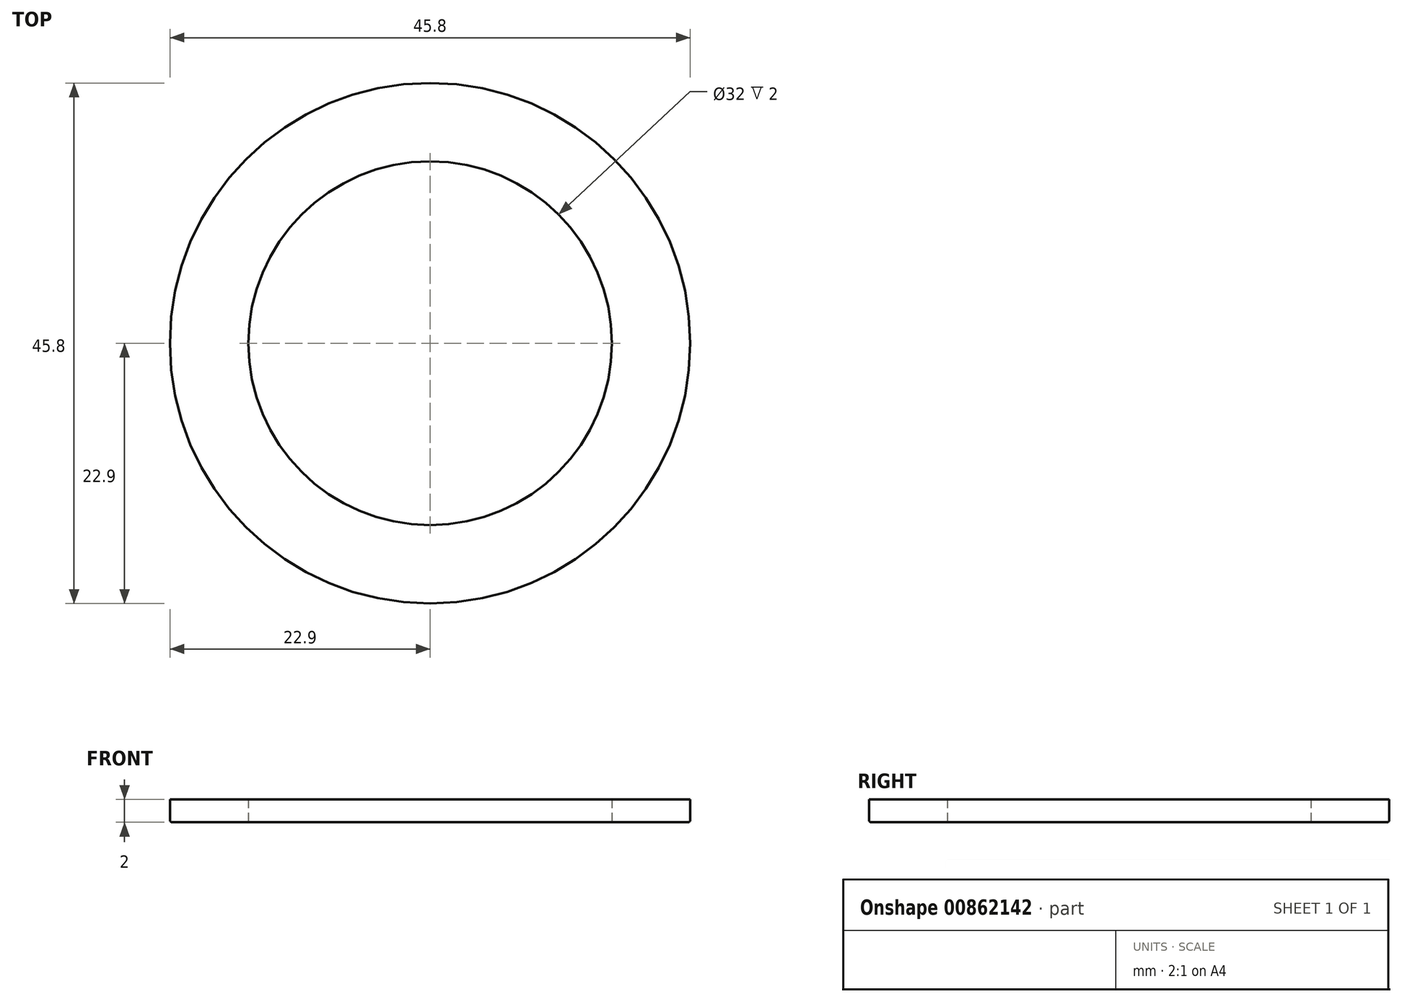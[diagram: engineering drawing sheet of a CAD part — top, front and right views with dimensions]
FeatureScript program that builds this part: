
annotation { "Feature Type Name" : "Feature", "Feature Type Description" : "" }
export const myFeature = defineFeature(function(context is Context, id is Id, definition is map)
    precondition{}
    {
        {
            var Q0;
            Q0=qCreatedBy(makeId("Top.planeOp"),FACE);
            var sketch = newSketch(context, id + "F0", { "sketchPlane" : qUnion([Q0])});
            skCircle(sketch, "E0", {"center": v(0, 0) * mm, "radius": 22.9 * mm});
            skSolve(sketch);
        }
        {
            var Q0;
            Q0 = qSketchRegion(id + "F0", true);
            extrude(context, id + "F1", {"entities" : qUnion([Q0]), "depth" : 2 * mm, "offsetDistance" : 25 * mm});
        }
        {
            var Q0;
            Q0=qCreatedBy(makeId("Top.planeOp"),FACE);
            var sketch = newSketch(context, id + "F2", { "sketchPlane" : qUnion([Q0])});
            skCircle(sketch, "E1", {"center": v(0, 0) * mm, "radius": 16 * mm});
            skSolve(sketch);
        }
        {
            var Q0;
            Q0 = qSketchRegion(id + "F2", true);
            extrude(context, id + "F3", {"entities" : qUnion([Q0]), "operationType" : NewBodyOperationType.REMOVE, "depth" : 2 * mm, "offsetDistance" : 25 * mm});
        }
        {
            var Q0;
            Q0=makeQuery(id+"F1.opExtrude","CAP_EDGE",EDGE,{"disambiguationData":[OSD([sQuery(id+"F0.wireOp",EDGE,"E0")])],"isStart":true});
            var Q1;
            Q1=makeQuery(id+"F3.boolean.opBoolean","COPY",EDGE,{"derivedFrom":makeQuery(id+"F3.opExtrude","CAP_EDGE",EDGE,{"disambiguationData":[OSD([sQuery(id+"F2.wireOp",EDGE,"E1")])],"isStart":true})});
            fillet(context, id + "F4", {"entities" : qUnion([Q0, Q1]), "radius" : 0.2 * mm, "tangentPropagation" : true, "allowEdgeOverflow" : false});
        }
    });
